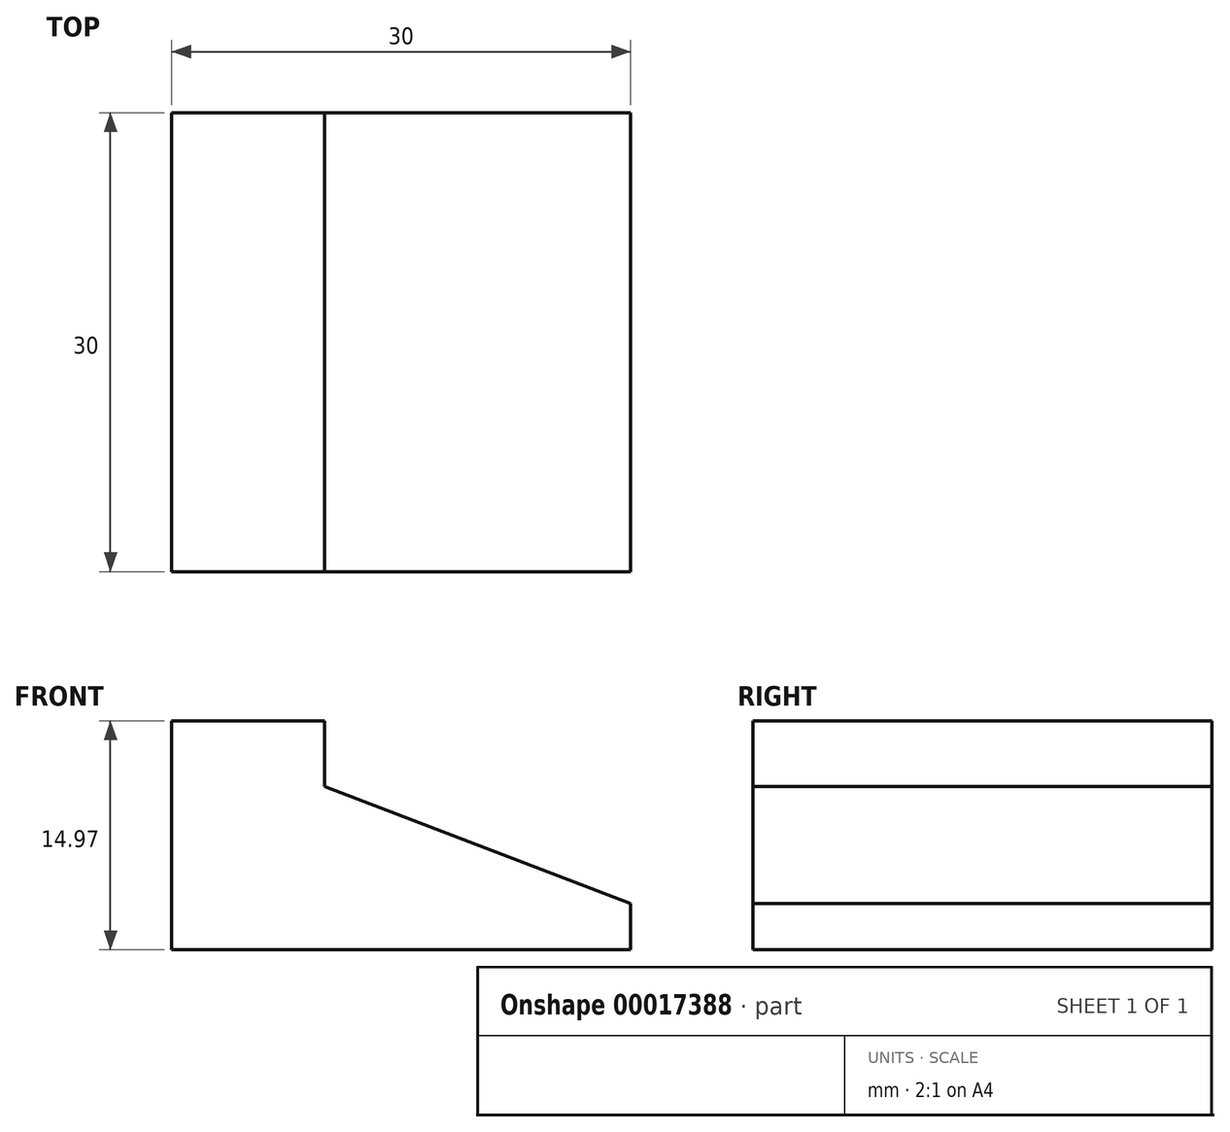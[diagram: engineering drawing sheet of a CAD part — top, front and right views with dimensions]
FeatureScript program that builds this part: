
annotation { "Feature Type Name" : "Feature", "Feature Type Description" : "" }
export const myFeature = defineFeature(function(context is Context, id is Id, definition is map)
    precondition{}
    {
        {
            var Q0;
            Q0=qCreatedBy(makeId("Front.planeOp"),FACE);
            var sketch = newSketch(context, id + "F0", { "sketchPlane" : qUnion([Q0])});
            skLineSegment(sketch, "E0", {"start": v(-10, 7.46) * mm, "end": v(-10, -7.51) * mm});
            skLineSegment(sketch, "E1", {"start": v(-10, -7.51) * mm, "end": v(20, -7.51) * mm});
            skLineSegment(sketch, "E2", {"start": v(20, -7.51) * mm, "end": v(20, -4.48) * mm});
            skLineSegment(sketch, "E3", {"start": v(20, -4.48) * mm, "end": v(0, 3.15) * mm});
            skLineSegment(sketch, "E4", {"start": v(0, 3.15) * mm, "end": v(0, 6.94) * mm});
            skLineSegment(sketch, "E5", {"start": v(-10, 7.46) * mm, "end": v(0, 7.46) * mm});
            skLineSegment(sketch, "E6", {"start": v(0, 7.46) * mm, "end": v(0, 6.94) * mm});
            skSolve(sketch);
        }
        {
            var Q0;
            Q0=makeQuery(id+"F0.imprint","IMPRINT",FACE,{"disambiguationData":[TD([[makeQuery(id+"F0.imprint","IMPRINT",EDGE,{"derivedFrom":sQuery(id+"F0.wireOp",EDGE,"E0")}),1.0]])]});
            extrude(context, id + "F1", {"entities" : qUnion([Q0]), "depth" : 30 * mm});
        }
    });
